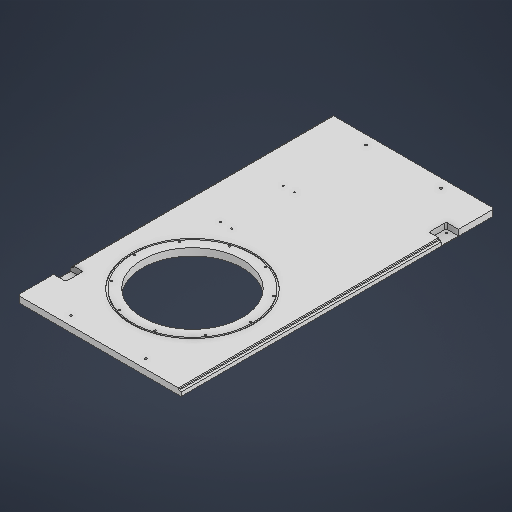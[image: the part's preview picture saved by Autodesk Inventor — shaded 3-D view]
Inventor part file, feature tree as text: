
AUTODESK INVENTOR PART (.ipt)
format: ipt  version: 2025 (Build 290162000, 162)  size: 397,312 bytes
history: native  units: in
note: dims shown in document units (in); Inventor stores cm internally (conversion verified against a paired STEP export)
features: sketch x10, extrude x5, chamfer x5, hole x4, plane x1, fillet x1
ambient origin geometry x8: Origin, YZ Plane, XZ Plane, XY Plane, X Axis, Y Axis, Z Axis, Center Point
bodies: Solid1 (feature_tree)
feature tree (26):
  extrude  "Extrusion1"  Depth=27.1654in
  sketch  "Sketch2"  dims[d2=0.625in d3=0.0in d4=8.0709in]
  extrude  "Extrusion2"  Depth=0.625in
  hole  "Hole2"  [1 undecoded]
  plane  "Work Plane1"
  hole  "Hole3"  [1 undecoded]
  extrude  "Extrusion6"  Depth=0.1575in
  hole  "Hole4"  [1 undecoded]
  sketch  "Sketch9"  dims[d49=5.4331in]
  fillet  "Fillet2"  Radius=0.9843in
  chamfer  "Chamfer1"  Distance=25.5906in
  chamfer  "Chamfer2"  Distance=10.3543in
  extrude  "Extrusion7"  Depth=0.1299in
  extrude  "Extrusion8"  Depth=0.0984in TaperAngle=0.0deg
  chamfer  "Chamfer3"  Distance=10.0394in
  chamfer  "Chamfer4"  Distance=0.1575in
  hole  "Hole5"  [1 undecoded]
  chamfer  "Chamfer5"  Distance=1.063in
  sketch  "Sketch1"  dims[d0=14.1732in d1=27.1654in]
  sketch  "Sketch4"  dims[d5=8.6614in d6=0.0in d7=0.0in]
  sketch  "Sketch6"  dims[d37=7.4409in d38=0.1575in]
  sketch  "Sketch7"  dims[d39=0.1575in d40=0.9843in]
  sketch  "Sketch8"  dims[d41=0.1276in d42=0.3937in d43=0.1575in d44=0.0787in d45=90.0deg d46=0.3937in d47=0.8108in d48=0.9843in]
  sketch  "Sketch Circular Pattern4"  dims[d8=10.6299in d36=3.3071in]
  sketch  "Sketch10"  dims[d50=5.9055in]
  sketch  "Sketch11"  dims[d55=6.5in d56=25.5906in d57=0.1936in d58=0.1969in d59=0.1575in d60=0.0787in d61=90.0deg d62=0.1969in d63=0.8108in d64=10.3543in d65=10.6299in d66=0.0984in d67=0.0in d68=10.0394in d69=0.1575in d70=3.937in d72=360.0deg d74=0.1628in d75=0.3937in d76=0.1575in d77=0.0787in d78=90.0deg d79=0.3937in d80=0.8108in d82=1.063in d83=1.063in d84=1.4961in d85=1.4961in d86=3.1102in d87=3.1102in d88=0.1969in d89=0.0984in d90=0.0787in d91=45.0deg d92=0.0984in d93=0.0787in d94=45.0deg d95=0.1181in d96=0.1181in d97=0.4951in d98=0.0in d99=0.2362in d100=0.2362in d101=0.122in d102=0.0in d103=0.0787in d104=0.1378in d105=45.0deg d106=0.1378in d107=0.0787in d108=45.0deg d109=0.748in d110=0.315in d111=0.8661in d112=0.748in d113=0.1299in d114=0.1299in d115=0.1299in d116=0.1299in d118=0.315in d119=0.8661in d120=0.748in d121=0.748in d122=0.1276in d123=0.315in d124=0.1575in d125=0.0787in d126=90.0deg d127=0.315in d128=0.8108in d129=0.0138in d130=0.0787in d131=45.0deg d26=0.0394in d27=0.0394in d28=0.0394in d29=0.0059in d30=0.0098in d31=0.0148in d32=0.5635in d33=0.0295in d34=0.8108in d35=0.0025in]
note: 4 required parameter values undecoded (feature->parameter linkage not recoverable at this tier; creation-order binding heuristic only, values carry confidence <= 0.55)
